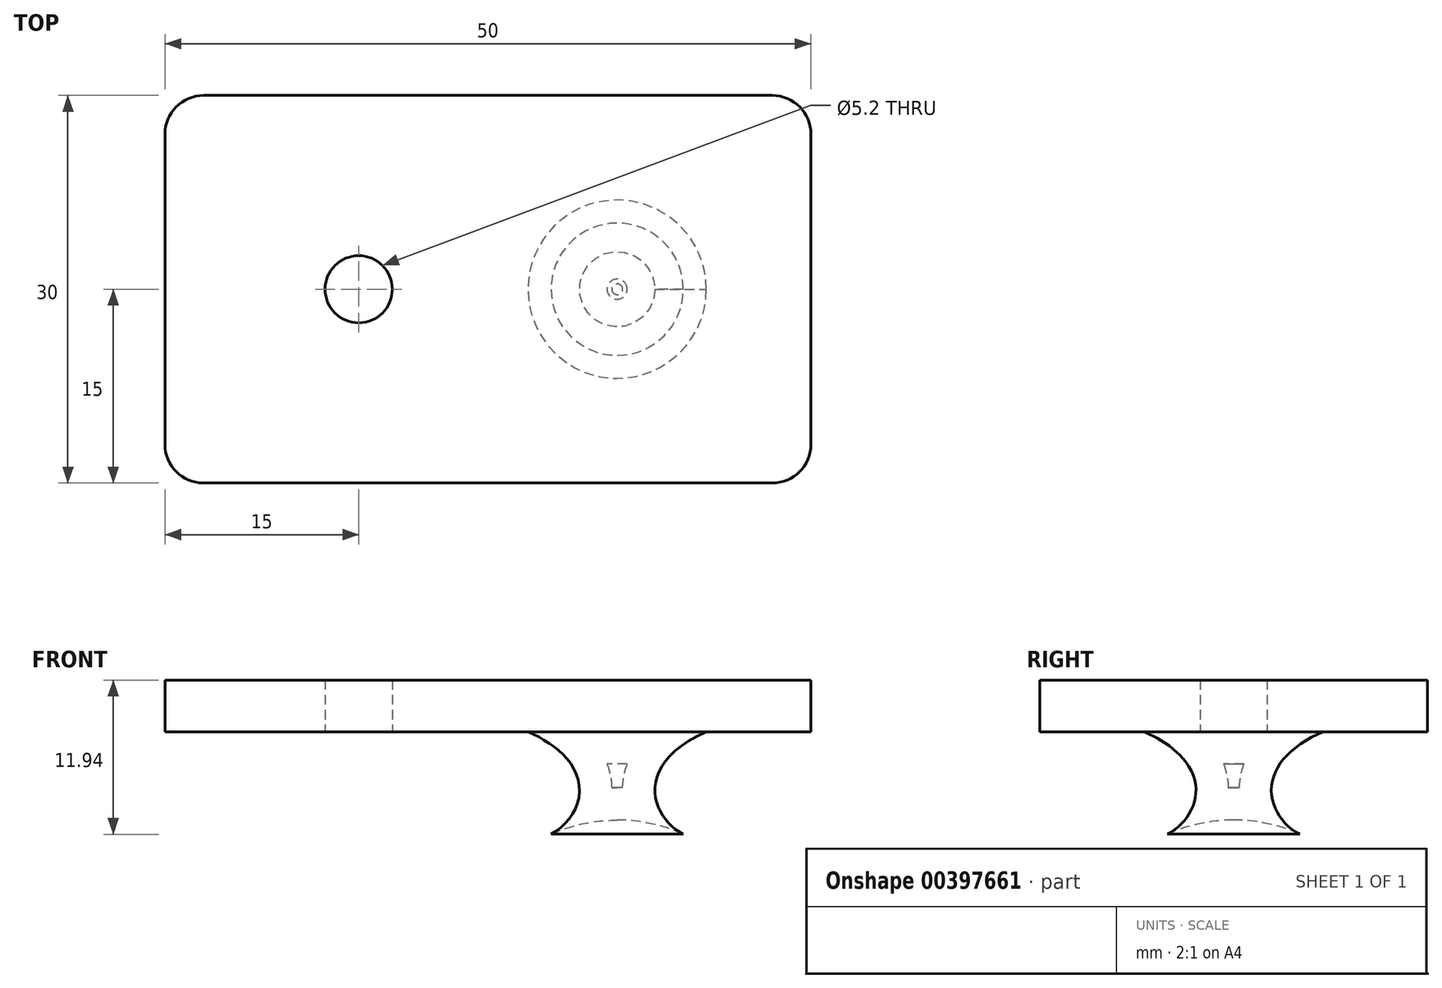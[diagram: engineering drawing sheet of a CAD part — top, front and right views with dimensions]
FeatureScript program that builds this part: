
annotation { "Feature Type Name" : "Feature", "Feature Type Description" : "" }
export const myFeature = defineFeature(function(context is Context, id is Id, definition is map)
    precondition{}
    {
        {
            var Q0;
            Q0=qCreatedBy(makeId("Front.planeOp"),FACE);
            var sketch = newSketch(context, id + "F0", { "sketchPlane" : qUnion([Q0])});
            skLineSegment(sketch, "E0", {"start": v(0, 0) * mm, "end": v(0, -36.84) * mm});
            skArc(sketch, "E1", {"start": v(0, -11.84) * mm, "mid": v(-12.5, -24.34) * mm, "end": v(0, -36.84) * mm});
            skLineSegment(sketch, "E2", {"start": v(0, -5) * mm, "end": v(-6.9, -5) * mm});
            skLineSegment(sketch, "E3", {"start": v(0, -13) * mm, "end": v(-5.25, -13) * mm, "construction": true});
            skFitSpline(sketch, "E4", {"points": [v(-5.25, -13) * mm, v(-6.9, -5) * mm], "startDerivative": vector(7.3, 3.37) * mm, "endDerivative": vector(-17.96, 8.1) * mm});
            skSolve(sketch);
        }
        {
            var Q0;
            {var subQ0=sQuery(id+"F0.wireOp",EDGE,"E1");var subQ1=sQuery(id+"F0.wireOp",EDGE,"E0");var subQ2=makeQuery(id+"F0.imprint","INTERSECT",VERTEX,{"disambiguationData":[OD(0.0)],"derivedFrom":[subQ1,subQ0]});Q0=makeQuery(id+"F0.imprint","IMPRINT",FACE,{"disambiguationData":[TD([[makeQuery(id+"F0.imprint","IMPRINT",EDGE,{"disambiguationData":[TD([[subQ2,1.0]])],"derivedFrom":subQ1}),-1.0]])]});}
            var Q1;
            {var subQ3=sQuery(id+"F0.wireOp",EDGE,"E2");Q1=makeQuery(id+"F0.imprint","IMPRINT",FACE,{"disambiguationData":[TD([[makeQuery(id+"F0.imprint","IMPRINT",EDGE,{"derivedFrom":subQ3}),1.0]])]});}
            var Q2;
            Q2=sQuery(id+"F0.wireOp",EDGE,"E0");
            revolve(context, id + "F1", {"entities" : qUnion([Q0, Q1]), "axis" : qUnion([Q2]), "revolveType" : RevolveType.FULL});
        }
        {
            var Q0;
            Q0=makeQuery(id+"F1.opRevolve","SWEPT_FACE",FACE,{"disambiguationData":[OSD([sQuery(id+"F0.wireOp",EDGE,"E1")])]});
            var Q1;
            Q1=makeQuery(id+"F1.opRevolve","SWEPT_FACE",FACE,{"disambiguationData":[OSD([sQuery(id+"F0.wireOp",EDGE,"E4")])]});
            var Q2;
            Q2=makeQuery(id+"F1.opRevolve","SWEPT_BODY",BODY,{"disambiguationData":[OSD([sQuery(id+"F0.wireOp",EDGE,"E0"),sQuery(id+"F0.wireOp",EDGE,"E1"),sQuery(id+"F0.wireOp",EDGE,"E2"),sQuery(id+"F0.wireOp",EDGE,"E4")])]});
            shell(context, id + "F2", {"isHollow" : true, "entities" : qUnion([Q0, Q1]), "parts" : qUnion([Q2]), "thickness" : 2.5 * mm});
        }
        {
            var Q0;
            Q0=makeQuery(id+"F1.opRevolve","SWEPT_FACE",FACE,{"disambiguationData":[OSD([sQuery(id+"F0.wireOp",EDGE,"E2")])]});
            var sketch = newSketch(context, id + "F3", { "sketchPlane" : qUnion([Q0])});
            skPoint(sketch, "E5", {"position": v(0, 0) * mm});
            skLineSegment(sketch, "E6.bottom", {"start": v(12, -15) * mm, "end": v(-32, -15) * mm});
            skLineSegment(sketch, "E6.top", {"start": v(12, 15) * mm, "end": v(-32, 15) * mm});
            skLineSegment(sketch, "E6.left", {"start": v(15, -12) * mm, "end": v(15, 12) * mm});
            skLineSegment(sketch, "E6.right", {"start": v(-35, -12) * mm, "end": v(-35, 12) * mm});
            skPoint(sketch, "E7.visualSharp", {"position": v(15, -15) * mm});
            skArc(sketch, "E7.filletArc", {"start": v(12, -15) * mm, "mid": v(14.12, -14.12) * mm, "end": v(15, -12) * mm});
            skPoint(sketch, "E8.visualSharp", {"position": v(15, 15) * mm});
            skArc(sketch, "E8.filletArc", {"start": v(15, 12) * mm, "mid": v(14.12, 14.12) * mm, "end": v(12, 15) * mm});
            skPoint(sketch, "E9.visualSharp", {"position": v(-35, 15) * mm});
            skArc(sketch, "E9.filletArc", {"start": v(-32, 15) * mm, "mid": v(-34.12, 14.12) * mm, "end": v(-35, 12) * mm});
            skPoint(sketch, "E10.visualSharp", {"position": v(-35, -15) * mm});
            skArc(sketch, "E10.filletArc", {"start": v(-35, -12) * mm, "mid": v(-34.12, -14.12) * mm, "end": v(-32, -15) * mm});
            skCircle(sketch, "E11", {"center": v(-20, 0) * mm, "radius": 2.6 * mm});
            skSolve(sketch);
        }
        {
            var Q0;
            Q0 = qSketchRegion(id + "F3", true);
            extrude(context, id + "F4", {"entities" : qUnion([Q0]), "operationType" : NewBodyOperationType.ADD, "depth" : 4 * mm});
        }
    });
